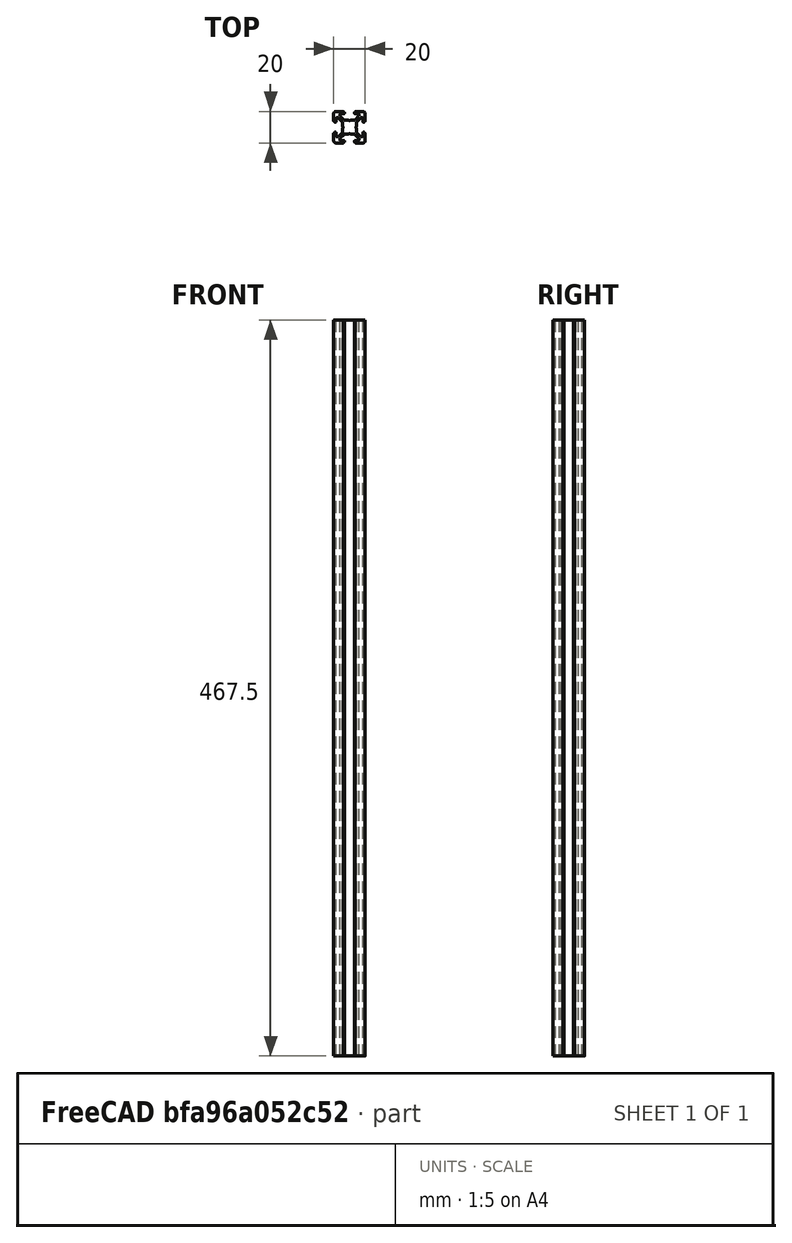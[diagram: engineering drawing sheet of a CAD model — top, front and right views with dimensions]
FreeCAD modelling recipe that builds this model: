
FCSTD DOCUMENT  (FreeCAD 0.15R4671 (Git))
Label: Perfil vertical 467,5 mm
License: CC-BY 3.0
LicenseURL: http://creativecommons.org/licenses/by/3.0/
objects: Sketcher::SketchObject×2, PartDesign::Pad×1, PartDesign::Pocket×1, Part::MultiFuse×1
note: 7 computed .brp shape members not serialized (recipe doc carries the construction recipe); baked Part::Feature solids carry a one-line shape summary decoded from their .brp

FEATURE [Sketcher::SketchObject] Sketch
  Placement = pos=(1.5,0,0) rot=(0,0,1;0rad)
  sketch-geometry (136):
    g0: LineSegment StartX=0 StartY=20 StartZ=0 EndX=4.65 EndY=20 EndZ=0
    g1: ArcOfCircle CenterX=-1e-12 CenterY=18.5 CenterZ=0 NormalX=0 NormalY=0 NormalZ=1 Radius=1.5 StartAngle=1.5708 EndAngle=3.14159
    g2: LineSegment StartX=-1.5 StartY=13.85 StartZ=0 EndX=-1.5 EndY=18.5 EndZ=0
    g3: ArcOfCircle CenterX=-1.3 CenterY=13.85 CenterZ=0 NormalX=0 NormalY=0 NormalZ=1 Radius=0.2 StartAngle=3.14159 EndAngle=4.71239
    g4: LineSegment StartX=-1 StartY=13.65 StartZ=0 EndX=-1.3 EndY=13.65 EndZ=0
    g5: LineSegment StartX=-1 StartY=13.3 StartZ=0 EndX=-1 EndY=13.65 EndZ=0
    g6: ArcOfCircle CenterX=-0.8 CenterY=13.3 CenterZ=0 NormalX=0 NormalY=0 NormalZ=1 Radius=0.2 StartAngle=3.14159 EndAngle=4.71239
    g7: LineSegment StartX=-0.5 StartY=13.1 StartZ=0 EndX=-0.8 EndY=13.1 EndZ=0
    g8: ArcOfCircle CenterX=-0.5 CenterY=13.6 CenterZ=0 NormalX=0 NormalY=0 NormalZ=1 Radius=0.5 StartAngle=4.71239 EndAngle=6.28319
    g9: LineSegment StartX=2.68e-07 StartY=15.5 StartZ=0 EndX=2.68e-07 EndY=13.6 EndZ=0
    g10: ArcOfCircle CenterX=0.5 CenterY=15.5 CenterZ=0 NormalX=0 NormalY=0 NormalZ=1 Radius=0.5 StartAngle=1.5708 EndAngle=3.14159
    g11: LineSegment StartX=1.23223 StartY=16 StartZ=0 EndX=0.5 EndY=16 EndZ=0
    g12: ArcOfCircle CenterX=1.23223 CenterY=15.5 CenterZ=0 NormalX=0 NormalY=0 NormalZ=1 Radius=0.5 StartAngle=0.785398 EndAngle=1.5708
    g13: LineSegment StartX=3.85355 StartY=13.5858 StartZ=0 EndX=1.58579 EndY=15.8536 EndZ=0
    g14: ArcOfCircle CenterX=3.5 CenterY=13.2322 CenterZ=0 NormalX=0 NormalY=0 NormalZ=1 Radius=0.5 StartAngle=0 EndAngle=0.785398
    g15: LineSegment StartX=4 StartY=10.9536 StartZ=0 EndX=4 EndY=13.2322 EndZ=0
    g16: ArcOfCircle CenterX=4.2 CenterY=10.9536 CenterZ=0 NormalX=0 NormalY=0 NormalZ=1 Radius=0.2 StartAngle=3.14159 EndAngle=3.66519
    g17: LineSegment StartX=4.46188 StartY=10.1 StartZ=0 EndX=4.0268 EndY=10.8536 EndZ=0
    g18: ArcOfCircle CenterX=4.28868 CenterY=10 CenterZ=0 NormalX=0 NormalY=0 NormalZ=1 Radius=0.2 StartAngle=5.75959 EndAngle=6.80678
    g19: LineSegment StartX=4.0268 StartY=9.14641 StartZ=0 EndX=4.46188 EndY=9.9 EndZ=0
    g20: ArcOfCircle CenterX=4.2 CenterY=9.04641 CenterZ=0 NormalX=0 NormalY=0 NormalZ=1 Radius=0.2 StartAngle=2.61799 EndAngle=3.14159
    g21: LineSegment StartX=4 StartY=6.76777 StartZ=0 EndX=4 EndY=9.04641 EndZ=0
    g22: ArcOfCircle CenterX=3.5 CenterY=6.76777 CenterZ=0 NormalX=0 NormalY=0 NormalZ=1 Radius=0.5 StartAngle=5.49779 EndAngle=6.28319
    g23: LineSegment StartX=1.58579 StartY=4.14645 StartZ=0 EndX=3.85355 EndY=6.41421 EndZ=0
    g24: ArcOfCircle CenterX=1.23223 CenterY=4.5 CenterZ=0 NormalX=0 NormalY=0 NormalZ=1 Radius=0.5 StartAngle=4.71239 EndAngle=5.49779
    g25: LineSegment StartX=0.5 StartY=4 StartZ=0 EndX=1.23223 EndY=4 EndZ=0
    g26: ArcOfCircle CenterX=0.5 CenterY=4.5 CenterZ=0 NormalX=0 NormalY=0 NormalZ=1 Radius=0.5 StartAngle=3.14159 EndAngle=4.71239
    g27: LineSegment StartX=2.68e-07 StartY=6.4 StartZ=0 EndX=2.68e-07 EndY=4.5 EndZ=0
    g28: ArcOfCircle CenterX=-0.5 CenterY=6.4 CenterZ=0 NormalX=0 NormalY=0 NormalZ=1 Radius=0.5 StartAngle=0 EndAngle=1.5708
    g29: LineSegment StartX=-0.8 StartY=6.9 StartZ=0 EndX=-0.5 EndY=6.9 EndZ=0
    g30: ArcOfCircle CenterX=-0.8 CenterY=6.7 CenterZ=0 NormalX=0 NormalY=0 NormalZ=1 Radius=0.2 StartAngle=1.5708 EndAngle=3.14159
    g31: LineSegment StartX=-1 StartY=6.35 StartZ=0 EndX=-1 EndY=6.7 EndZ=0
    g32: LineSegment StartX=-1.3 StartY=6.35 StartZ=0 EndX=-1 EndY=6.35 EndZ=0
    g33: ArcOfCircle CenterX=-1.3 CenterY=6.15 CenterZ=0 NormalX=0 NormalY=0 NormalZ=1 Radius=0.2 StartAngle=1.5708 EndAngle=3.14159
    g34: LineSegment StartX=-1.5 StartY=1.5 StartZ=0 EndX=-1.5 EndY=6.15 EndZ=0
    g35: ArcOfCircle CenterX=0 CenterY=1.5 CenterZ=0 NormalX=0 NormalY=0 NormalZ=1 Radius=1.5 StartAngle=3.14159 EndAngle=4.71239
    g36: LineSegment StartX=4.65 StartY=1e-12 StartZ=0 EndX=0 EndY=0 EndZ=0
    g37: ArcOfCircle CenterX=4.65 CenterY=0.2 CenterZ=0 NormalX=0 NormalY=0 NormalZ=1 Radius=0.2 StartAngle=4.71239 EndAngle=6.28319
    g38: LineSegment StartX=4.85 StartY=0.5 StartZ=0 EndX=4.85 EndY=0.2 EndZ=0
    g39: LineSegment StartX=5.2 StartY=0.5 StartZ=0 EndX=4.85 EndY=0.5 EndZ=0
    g40: ArcOfCircle CenterX=5.2 CenterY=0.7 CenterZ=0 NormalX=0 NormalY=0 NormalZ=1 Radius=0.2 StartAngle=4.71239 EndAngle=6.28319
    g41: LineSegment StartX=5.4 StartY=1 StartZ=0 EndX=5.4 EndY=0.7 EndZ=0
    g42: ArcOfCircle CenterX=4.9 CenterY=1 CenterZ=0 NormalX=0 NormalY=0 NormalZ=1 Radius=0.5 StartAngle=0 EndAngle=1.5708
    g43: LineSegment StartX=3 StartY=1.5 StartZ=0 EndX=4.9 EndY=1.5 EndZ=0
    g44: ArcOfCircle CenterX=3 CenterY=2 CenterZ=0 NormalX=0 NormalY=0 NormalZ=1 Radius=0.5 StartAngle=3.14159 EndAngle=4.71239
    g45: LineSegment StartX=2.5 StartY=2.73223 StartZ=0 EndX=2.5 EndY=2 EndZ=0
    g46: ArcOfCircle CenterX=3 CenterY=2.73223 CenterZ=0 NormalX=0 NormalY=0 NormalZ=1 Radius=0.5 StartAngle=2.35619 EndAngle=3.14159
    g47: LineSegment StartX=4.91421 StartY=5.35355 StartZ=0 EndX=2.64645 EndY=3.08579 EndZ=0
    g48: ArcOfCircle CenterX=5.26777 CenterY=5 CenterZ=0 NormalX=0 NormalY=0 NormalZ=1 Radius=0.5 StartAngle=1.5708 EndAngle=2.35619
    g49: LineSegment StartX=7.54641 StartY=5.5 StartZ=0 EndX=5.26777 EndY=5.5 EndZ=0
    g50: ArcOfCircle CenterX=7.54641 CenterY=5.7 CenterZ=0 NormalX=0 NormalY=0 NormalZ=1 Radius=0.2 StartAngle=4.71239 EndAngle=5.23599
    g51: LineSegment StartX=8.4 StartY=5.96188 StartZ=0 EndX=7.64641 EndY=5.52679 EndZ=0
    g52: ArcOfCircle CenterX=8.5 CenterY=5.78868 CenterZ=0 NormalX=0 NormalY=0 NormalZ=1 Radius=0.2 StartAngle=1.0472 EndAngle=2.0944
    g53: LineSegment StartX=9.35359 StartY=5.52679 StartZ=0 EndX=8.6 EndY=5.96188 EndZ=0
    g54: ArcOfCircle CenterX=9.45359 CenterY=5.7 CenterZ=0 NormalX=0 NormalY=0 NormalZ=1 Radius=0.2 StartAngle=4.18879 EndAngle=4.71239
    g55: LineSegment StartX=11.7322 StartY=5.5 StartZ=0 EndX=9.45359 EndY=5.5 EndZ=0
    g56: ArcOfCircle CenterX=11.7322 CenterY=5 CenterZ=0 NormalX=0 NormalY=0 NormalZ=1 Radius=0.5 StartAngle=0.785398 EndAngle=1.5708
    g57: LineSegment StartX=14.3536 StartY=3.08579 StartZ=0 EndX=12.0858 EndY=5.35355 EndZ=0
    g58: ArcOfCircle CenterX=14 CenterY=2.73223 CenterZ=0 NormalX=0 NormalY=0 NormalZ=1 Radius=0.5 StartAngle=0 EndAngle=0.785398
    g59: LineSegment StartX=14.5 StartY=2 StartZ=0 EndX=14.5 EndY=2.73223 EndZ=0
    g60: ArcOfCircle CenterX=14 CenterY=2 CenterZ=0 NormalX=0 NormalY=0 NormalZ=1 Radius=0.5 StartAngle=4.71239 EndAngle=6.28319
    g61: LineSegment StartX=12.1 StartY=1.5 StartZ=0 EndX=14 EndY=1.5 EndZ=0
    g62: ArcOfCircle CenterX=12.1 CenterY=1 CenterZ=0 NormalX=0 NormalY=0 NormalZ=1 Radius=0.5 StartAngle=1.5708 EndAngle=3.14159
    g63: LineSegment StartX=11.6 StartY=0.7 StartZ=0 EndX=11.6 EndY=1 EndZ=0
    g64: ArcOfCircle CenterX=11.8 CenterY=0.7 CenterZ=0 NormalX=0 NormalY=0 NormalZ=1 Radius=0.2 StartAngle=3.14159 EndAngle=4.71239
    g65: LineSegment StartX=12.15 StartY=0.5 StartZ=0 EndX=11.8 EndY=0.5 EndZ=0
    g66: LineSegment StartX=12.15 StartY=0.2 StartZ=0 EndX=12.15 EndY=0.5 EndZ=0
    g67: ArcOfCircle CenterX=12.35 CenterY=0.2 CenterZ=0 NormalX=0 NormalY=0 NormalZ=1 Radius=0.2 StartAngle=3.14159 EndAngle=4.71239
    g68: LineSegment StartX=17 StartY=1e-12 StartZ=0 EndX=12.35 EndY=0 EndZ=0
    g69: ArcOfCircle CenterX=17 CenterY=1.5 CenterZ=0 NormalX=0 NormalY=0 NormalZ=1 Radius=1.5 StartAngle=4.71239 EndAngle=6.28319
    g70: LineSegment StartX=18.5 StartY=6.15 StartZ=0 EndX=18.5 EndY=1.5 EndZ=0
    g71: ArcOfCircle CenterX=18.3 CenterY=6.15 CenterZ=0 NormalX=0 NormalY=0 NormalZ=1 Radius=0.2 StartAngle=0 EndAngle=1.5708
    g72: LineSegment StartX=18 StartY=6.35 StartZ=0 EndX=18.3 EndY=6.35 EndZ=0
    g73: LineSegment StartX=18 StartY=6.7 StartZ=0 EndX=18 EndY=6.35 EndZ=0
    g74: ArcOfCircle CenterX=17.8 CenterY=6.7 CenterZ=0 NormalX=0 NormalY=0 NormalZ=1 Radius=0.2 StartAngle=0 EndAngle=1.5708
    g75: LineSegment StartX=17.5 StartY=6.9 StartZ=0 EndX=17.8 EndY=6.9 EndZ=0
    g76: ArcOfCircle CenterX=17.5 CenterY=6.4 CenterZ=0 NormalX=0 NormalY=0 NormalZ=1 Radius=0.5 StartAngle=1.5708 EndAngle=3.14159
    g77: LineSegment StartX=17 StartY=4.5 StartZ=0 EndX=17 EndY=6.4 EndZ=0
    g78: ArcOfCircle CenterX=16.5 CenterY=4.5 CenterZ=0 NormalX=0 NormalY=0 NormalZ=1 Radius=0.5 StartAngle=4.71239 EndAngle=6.28319
    g79: LineSegment StartX=15.7678 StartY=4 StartZ=0 EndX=16.5 EndY=4 EndZ=0
    g80: ArcOfCircle CenterX=15.7678 CenterY=4.5 CenterZ=0 NormalX=0 NormalY=0 NormalZ=1 Radius=0.5 StartAngle=3.92699 EndAngle=4.71239
    g81: LineSegment StartX=13.1464 StartY=6.41421 StartZ=0 EndX=15.4142 EndY=4.14645 EndZ=0
    g82: ArcOfCircle CenterX=13.5 CenterY=6.76777 CenterZ=0 NormalX=0 NormalY=0 NormalZ=1 Radius=0.5 StartAngle=3.14159 EndAngle=3.92699
    g83: LineSegment StartX=13 StartY=9.04641 StartZ=0 EndX=13 EndY=6.76777 EndZ=0
    g84: ArcOfCircle CenterX=12.8 CenterY=9.04641 CenterZ=0 NormalX=0 NormalY=0 NormalZ=1 Radius=0.2 StartAngle=0 EndAngle=0.523599
    g85: LineSegment StartX=12.5381 StartY=9.9 StartZ=0 EndX=12.9732 EndY=9.14641 EndZ=0
    g86: ArcOfCircle CenterX=12.7113 CenterY=10 CenterZ=0 NormalX=0 NormalY=0 NormalZ=1 Radius=0.2 StartAngle=2.61799 EndAngle=3.66519
    g87: LineSegment StartX=12.9732 StartY=10.8536 StartZ=0 EndX=12.5381 EndY=10.1 EndZ=0
    g88: ArcOfCircle CenterX=12.8 CenterY=10.9536 CenterZ=0 NormalX=0 NormalY=0 NormalZ=1 Radius=0.2 StartAngle=5.75959 EndAngle=6.28319
    g89: LineSegment StartX=13 StartY=13.2322 StartZ=0 EndX=13 EndY=10.9536 EndZ=0
    g90: ArcOfCircle CenterX=13.5 CenterY=13.2322 CenterZ=0 NormalX=0 NormalY=0 NormalZ=1 Radius=0.5 StartAngle=2.35619 EndAngle=3.14159
    g91: LineSegment StartX=15.4142 StartY=15.8536 StartZ=0 EndX=13.1464 EndY=13.5858 EndZ=0
    g92: ArcOfCircle CenterX=15.7678 CenterY=15.5 CenterZ=0 NormalX=0 NormalY=0 NormalZ=1 Radius=0.5 StartAngle=1.5708 EndAngle=2.35619
    g93: LineSegment StartX=16.5 StartY=16 StartZ=0 EndX=15.7678 EndY=16 EndZ=0
    g94: ArcOfCircle CenterX=16.5 CenterY=15.5 CenterZ=0 NormalX=0 NormalY=0 NormalZ=1 Radius=0.5 StartAngle=0 EndAngle=1.5708
    g95: LineSegment StartX=17 StartY=13.6 StartZ=0 EndX=17 EndY=15.5 EndZ=0
    g96: ArcOfCircle CenterX=17.5 CenterY=13.6 CenterZ=0 NormalX=0 NormalY=0 NormalZ=1 Radius=0.5 StartAngle=3.14159 EndAngle=4.71239
    g97: LineSegment StartX=17.8 StartY=13.1 StartZ=0 EndX=17.5 EndY=13.1 EndZ=0
    g98: ArcOfCircle CenterX=17.8 CenterY=13.3 CenterZ=0 NormalX=0 NormalY=0 NormalZ=1 Radius=0.2 StartAngle=4.71239 EndAngle=6.28319
    g99: LineSegment StartX=18 StartY=13.65 StartZ=0 EndX=18 EndY=13.3 EndZ=0
    g100: LineSegment StartX=18.3 StartY=13.65 StartZ=0 EndX=18 EndY=13.65 EndZ=0
    g101: ArcOfCircle CenterX=18.3 CenterY=13.85 CenterZ=0 NormalX=0 NormalY=0 NormalZ=1 Radius=0.2 StartAngle=4.71239 EndAngle=6.28319
    g102: LineSegment StartX=18.5 StartY=18.5 StartZ=0 EndX=18.5 EndY=13.85 EndZ=0
    g103: ArcOfCircle CenterX=17 CenterY=18.5 CenterZ=0 NormalX=0 NormalY=0 NormalZ=1 Radius=1.5 StartAngle=0 EndAngle=1.5708
    g104: LineSegment StartX=12.35 StartY=20 StartZ=0 EndX=17 EndY=20 EndZ=0
    g105: ArcOfCircle CenterX=12.35 CenterY=19.8 CenterZ=0 NormalX=0 NormalY=0 NormalZ=1 Radius=0.2 StartAngle=1.5708 EndAngle=3.14159
    g106: LineSegment StartX=12.15 StartY=19.5 StartZ=0 EndX=12.15 EndY=19.8 EndZ=0
    g107: LineSegment StartX=11.8 StartY=19.5 StartZ=0 EndX=12.15 EndY=19.5 EndZ=0
    g108: ArcOfCircle CenterX=11.8 CenterY=19.3 CenterZ=0 NormalX=0 NormalY=0 NormalZ=1 Radius=0.2 StartAngle=1.5708 EndAngle=3.14159
    g109: LineSegment StartX=11.6 StartY=19 StartZ=0 EndX=11.6 EndY=19.3 EndZ=0
    g110: ArcOfCircle CenterX=12.1 CenterY=19 CenterZ=0 NormalX=0 NormalY=0 NormalZ=1 Radius=0.5 StartAngle=3.14159 EndAngle=4.71239
    g111: LineSegment StartX=14 StartY=18.5 StartZ=0 EndX=12.1 EndY=18.5 EndZ=0
    g112: ArcOfCircle CenterX=14 CenterY=18 CenterZ=0 NormalX=0 NormalY=0 NormalZ=1 Radius=0.5 StartAngle=0 EndAngle=1.5708
    g113: LineSegment StartX=14.5 StartY=17.2678 StartZ=0 EndX=14.5 EndY=18 EndZ=0
    g114: ArcOfCircle CenterX=14 CenterY=17.2678 CenterZ=0 NormalX=0 NormalY=0 NormalZ=1 Radius=0.5 StartAngle=5.49779 EndAngle=6.28319
    g115: LineSegment StartX=12.0858 StartY=14.6464 StartZ=0 EndX=14.3536 EndY=16.9142 EndZ=0
    g116: ArcOfCircle CenterX=11.7322 CenterY=15 CenterZ=0 NormalX=0 NormalY=0 NormalZ=1 Radius=0.5 StartAngle=4.71239 EndAngle=5.49779
    g117: LineSegment StartX=9.45359 StartY=14.5 StartZ=0 EndX=11.7322 EndY=14.5 EndZ=0
    g118: ArcOfCircle CenterX=9.45359 CenterY=14.3 CenterZ=0 NormalX=0 NormalY=0 NormalZ=1 Radius=0.2 StartAngle=1.5708 EndAngle=2.0944
    g119: LineSegment StartX=8.6 StartY=14.0381 StartZ=0 EndX=9.35359 EndY=14.4732 EndZ=0
    g120: ArcOfCircle CenterX=8.5 CenterY=14.2113 CenterZ=0 NormalX=0 NormalY=0 NormalZ=1 Radius=0.2 StartAngle=4.18879 EndAngle=5.23599
    g121: LineSegment StartX=7.64641 StartY=14.4732 StartZ=0 EndX=8.4 EndY=14.0381 EndZ=0
    g122: ArcOfCircle CenterX=7.54641 CenterY=14.3 CenterZ=0 NormalX=0 NormalY=0 NormalZ=1 Radius=0.2 StartAngle=1.0472 EndAngle=1.5708
    g123: LineSegment StartX=5.26777 StartY=14.5 StartZ=0 EndX=7.54641 EndY=14.5 EndZ=0
    g124: ArcOfCircle CenterX=5.26777 CenterY=15 CenterZ=0 NormalX=0 NormalY=0 NormalZ=1 Radius=0.5 StartAngle=3.92699 EndAngle=4.71239
    g125: LineSegment StartX=2.64645 StartY=16.9142 StartZ=0 EndX=4.91421 EndY=14.6464 EndZ=0
    g126: ArcOfCircle CenterX=3 CenterY=17.2678 CenterZ=0 NormalX=0 NormalY=0 NormalZ=1 Radius=0.5 StartAngle=3.14159 EndAngle=3.92699
    g127: LineSegment StartX=2.5 StartY=18 StartZ=0 EndX=2.5 EndY=17.2678 EndZ=0
    g128: ArcOfCircle CenterX=3 CenterY=18 CenterZ=0 NormalX=0 NormalY=0 NormalZ=1 Radius=0.5 StartAngle=1.5708 EndAngle=3.14159
    g129: LineSegment StartX=4.9 StartY=18.5 StartZ=0 EndX=3 EndY=18.5 EndZ=0
    g130: ArcOfCircle CenterX=4.9 CenterY=19 CenterZ=0 NormalX=0 NormalY=0 NormalZ=1 Radius=0.5 StartAngle=4.71239 EndAngle=6.28319
    g131: LineSegment StartX=5.4 StartY=19.3 StartZ=0 EndX=5.4 EndY=19 EndZ=0
    g132: ArcOfCircle CenterX=5.2 CenterY=19.3 CenterZ=0 NormalX=0 NormalY=0 NormalZ=1 Radius=0.2 StartAngle=0 EndAngle=1.5708
    g133: LineSegment StartX=4.85 StartY=19.5 StartZ=0 EndX=5.2 EndY=19.5 EndZ=0
    g134: LineSegment StartX=4.85 StartY=19.8 StartZ=0 EndX=4.85 EndY=19.5 EndZ=0
    g135: ArcOfCircle CenterX=4.65 CenterY=19.8 CenterZ=0 NormalX=0 NormalY=0 NormalZ=1 Radius=0.2 StartAngle=0 EndAngle=1.5708
  constraints (136):
    c: Coincident(g0,g1)
    c: Coincident(g135,g0)
    c: Coincident(g1,g2)
    c: Coincident(g2,g3)
    c: Coincident(g3,g4)
    c: Coincident(g4,g5)
    c: Coincident(g6,g5)
    c: Coincident(g7,g6)
    c: Coincident(g8,g7)
    c: Coincident(g9,g8)
    c: Coincident(g10,g9)
    c: Coincident(g10,g11)
    c: Coincident(g11,g12)
    c: Coincident(g12,g13)
    c: Coincident(g14,g13)
    c: Coincident(g15,g14)
    c: Coincident(g15,g16)
    c: Coincident(g16,g17)
    c: Coincident(g17,g18)
    c: Coincident(g18,g19)
    c: Coincident(g19,g20)
    c: Coincident(g20,g21)
    c: Coincident(g21,g22)
    c: Coincident(g22,g23)
    c: Coincident(g23,g24)
    c: Coincident(g24,g25)
    c: Coincident(g26,g25)
    c: Coincident(g26,g27)
    c: Coincident(g28,g27)
    c: Coincident(g28,g29)
    c: Coincident(g30,g29)
    c: Coincident(g31,g30)
    c: Coincident(g31,g32)
    c: Coincident(g32,g33)
    c: Coincident(g33,g34)
    c: Coincident(g35,g34)
    c: Coincident(g36,g35)
    c: Coincident(g37,g36)
    c: Coincident(g37,g38)
    c: Coincident(g38,g39)
    c: Coincident(g40,g39)
    c: Coincident(g40,g41)
    c: Coincident(g41,g42)
    c: Coincident(g43,g42)
    c: Coincident(g44,g43)
    c: Coincident(g44,g45)
    c: Coincident(g45,g46)
    c: Coincident(g46,g47)
    c: Coincident(g47,g48)
    c: Coincident(g49,g48)
    c: Coincident(g49,g50)
    c: Coincident(g50,g51)
    c: Coincident(g51,g52)
    c: Coincident(g53,g52)
    c: Coincident(g54,g53)
    c: Coincident(g55,g54)
    c: Coincident(g56,g55)
    c: Coincident(g56,g57)
    c: Coincident(g58,g57)
    c: Coincident(g59,g58)
    c: Coincident(g60,g59)
    c: Coincident(g61,g60)
    c: Coincident(g62,g61)
    c: Coincident(g62,g63)
    c: Coincident(g64,g63)
    c: Coincident(g65,g64)
    c: Coincident(g66,g65)
    c: Coincident(g67,g66)
    c: Coincident(g67,g68)
    c: Coincident(g69,g68)
    c: Coincident(g70,g69)
    c: Coincident(g71,g70)
    c: Coincident(g72,g71)
    c: Coincident(g73,g72)
    c: Coincident(g73,g74)
    c: Coincident(g75,g74)
    c: Coincident(g76,g75)
    c: Coincident(g76,g77)
    c: Coincident(g77,g78)
    c: Coincident(g78,g79)
    c: Coincident(g80,g79)
    c: Coincident(g81,g80)
    c: Coincident(g81,g82)
    c: Coincident(g82,g83)
    c: Coincident(g83,g84)
    c: Coincident(g85,g84)
    c: Coincident(g86,g85)
    c: Coincident(g86,g87)
    c: Coincident(g88,g87)
    c: Coincident(g88,g89)
    c: Coincident(g89,g90)
    c: Coincident(g91,g90)
    c: Coincident(g92,g91)
    c: Coincident(g93,g92)
    c: Coincident(g94,g93)
    c: Coincident(g94,g95)
    c: Coincident(g95,g96)
    c: Coincident(g96,g97)
    c: Coincident(g98,g97)
    c: Coincident(g98,g99)
    c: Coincident(g100,g99)
    c: Coincident(g100,g101)
    c: Coincident(g101,g102)
    c: Coincident(g102,g103)
    c: Coincident(g103,g104)
    c: Coincident(g104,g105)
    c: Coincident(g106,g105)
    c: Coincident(g107,g106)
    c: Coincident(g108,g107)
    c: Coincident(g109,g108)
    c: Coincident(g110,g109)
    c: Coincident(g111,g110)
    c: Coincident(g112,g111)
    c: Coincident(g112,g113)
    c: Coincident(g113,g114)
    c: Coincident(g114,g115)
    c: Coincident(g115,g116)
    c: Coincident(g117,g116)
    c: Coincident(g118,g117)
    c: Coincident(g119,g118)
    c: Coincident(g119,g120)
    c: Coincident(g121,g120)
    c: Coincident(g121,g122)
    c: Coincident(g122,g123)
    c: Coincident(g124,g123)
    c: Coincident(g124,g125)
    c: Coincident(g126,g125)
    c: Coincident(g127,g126)
    c: Coincident(g128,g127)
    c: Coincident(g129,g128)
    c: Coincident(g130,g129)
    c: Coincident(g130,g131)
    c: Coincident(g131,g132)
    c: Coincident(g133,g132)
    c: Coincident(g134,g133)
    c: Coincident(g135,g134)
FEATURE [PartDesign::Pad] Pad
  Length = 467.5
  Length2 = 100
  Placement = pos=(1.5,0,0) rot=(0,0,1;0rad)
  Sketch = -> Sketch
  Type = 0
FEATURE [Sketcher::SketchObject] Sketch001
  Placement = pos=(1.5,0,467.5) rot=(0,0,1;0rad)
  Support = -> Pad [Face138]
  sketch-geometry (16):
    g0: ArcOfCircle CenterX=8.5 CenterY=10 CenterZ=0 NormalX=0 NormalY=0 NormalZ=1 Radius=3.54978 StartAngle=2.14023 EndAngle=2.57348
    g1: LineSegment StartX=6.5861 StartY=12.9896 StartZ=0 EndX=7.24181 EndY=12.4453 EndZ=0
    g2: ArcOfCircle CenterX=8.5 CenterY=10 CenterZ=0 NormalX=0 NormalY=0 NormalZ=1 Radius=2.75 StartAngle=1.09559 EndAngle=2.046
    g3: LineSegment StartX=9.75819 StartY=12.4453 StartZ=0 EndX=10.4139 EndY=12.9896 EndZ=0
    g4: ArcOfCircle CenterX=8.5 CenterY=10 CenterZ=0 NormalX=0 NormalY=0 NormalZ=1 Radius=3.54978 StartAngle=0.568112 EndAngle=1.00136
    g5: LineSegment StartX=11.4922 StartY=11.9099 StartZ=0 EndX=10.9453 EndY=11.2582 EndZ=0
    g6: ArcOfCircle CenterX=8.5 CenterY=10 CenterZ=0 NormalX=0 NormalY=0 NormalZ=1 Radius=2.75 StartAngle=5.80798 EndAngle=6.75839
    g7: LineSegment StartX=10.9453 StartY=8.74181 StartZ=0 EndX=11.4922 EndY=8.09007 EndZ=0
    g8: ArcOfCircle CenterX=8.5 CenterY=10 CenterZ=0 NormalX=0 NormalY=0 NormalZ=1 Radius=3.54978 StartAngle=5.28183 EndAngle=5.71507
    g9: LineSegment StartX=10.4139 StartY=7.01036 StartZ=0 EndX=9.75819 EndY=7.5547 EndZ=0
    g10: ArcOfCircle CenterX=8.5 CenterY=10 CenterZ=0 NormalX=0 NormalY=0 NormalZ=1 Radius=2.75 StartAngle=4.23718 EndAngle=5.1876
    g11: LineSegment StartX=7.24181 StartY=7.5547 StartZ=0 EndX=6.5861 EndY=7.01036 EndZ=0
    g12: ArcOfCircle CenterX=8.5 CenterY=10 CenterZ=0 NormalX=0 NormalY=0 NormalZ=1 Radius=3.54978 StartAngle=3.7097 EndAngle=4.14295
    g13: LineSegment StartX=5.50783 StartY=8.09007 StartZ=0 EndX=6.0547 EndY=8.74181 EndZ=0
    g14: ArcOfCircle CenterX=8.5 CenterY=10 CenterZ=0 NormalX=0 NormalY=0 NormalZ=1 Radius=2.75 StartAngle=2.66639 EndAngle=3.6168
    g15: LineSegment StartX=6.0547 StartY=11.2582 StartZ=0 EndX=5.50783 EndY=11.9099 EndZ=0
  constraints (16):
    c: Coincident(g0,g1)
    c: Coincident(g15,g0)
    c: Coincident(g1,g2)
    c: Coincident(g3,g2)
    c: Coincident(g4,g3)
    c: Coincident(g4,g5)
    c: Coincident(g6,g5)
    c: Coincident(g7,g6)
    c: Coincident(g8,g7)
    c: Coincident(g9,g8)
    c: Coincident(g10,g9)
    c: Coincident(g11,g10)
    c: Coincident(g12,g11)
    c: Coincident(g13,g12)
    c: Coincident(g14,g13)
    c: Coincident(g15,g14)
FEATURE [PartDesign::Pocket] Pocket
  Length = 5
  Placement = pos=(1.5,0,0) rot=(0,0,1;0rad)
  Sketch = -> Sketch001
  Type = 1
FEATURE [Part::MultiFuse] Fusion  label="Perfil vertical 467,5"
  Shapes = -> [Pocket,Pad]
